# Revit family: LAMP_FIL 70 PRISMATIC RECESSED
name_source: partatom
category: Luminarias
revit_build: Autodesk Revit 2015 (Build: 20140606_1530(x64)
units: mm (PartAtom-declared; Revit-internal decimal feet)

## types (16) — shared parameters
CRI = 80
Cambio de temperatura de color de luz atenuada = <Ninguno>
Comentarios de tipo = Availability of switching between accessories through visibility parameters when placed in a project.
Fabricante = LAMP
Filtro de color = 16777215
Gear = Electronic
IEE = A+
IFC Clasificación = Light Fixture
Installation instructions = https://www.lamp.es
Insulation class = I
LED Lifetime = 50.000 L80 B10
Last update = 14/08/2020
Luminaire type = Indoor - Modular System
Lámpara = LED MID-POWER
MacAdam = 3
Manufacturer URL = http://www.lamp.es
Manufacturer country = Spain
Manufacturer name = LAMP
Material Difusor = LAMP_PC Difusor Prismático Fil
Model explanation = Availability of switching between accessories through visibility parameters when placed in a project.
Power Supply = 220-240V 50-60Hz
Product URL = https://www.lamp.es
Product datasheet = https://www.lamp.es
Protection rating = IP42, IK06
Type = MID POWER PHILIPS
Ángulo de inclinación = 90,00°

## per-type parameters (varying)
| type | Archivo de red fotométrica | Descripción | Dimensions | Efficacy | Finish | Longitud | Longitud de línea de emisión | Material Perfil | Modelo | Plum | Power | Product code | Recessed dimensions | UniClass 1.4 Code | UniClass 2.0 Code | Weight |
| 1162MM 2600LM 3000K WHITE | 14741700.IES | FIL 70 PRISM REC 2600 WW WH. | 1162 x 89 x 70 mm | 114 lm/W | Matt white | 1162 mm  [stored 3.81234 ft] | 1162 mm  [stored 3.81234 ft] | LAMP_Aluminio Perfil Fil BL | F71RE120LOPR830NW | 19 W | 17 W | F71RE120LOPR830NW | 1174 x 78 x 85 mm | F71RE120LOPR830NW | F71RE120LOPR830NW | 2,77 kg |
| 1162MM 2600LM 3000K GREY | 14741703.IES | FIL 70 PRISM REC 2600 WW GR. | 1162 x 89 x 70 mm | 114 lm/W | Gloss grey | 1162 mm  [stored 3.81234 ft] | 1162 mm  [stored 3.81234 ft] | LAMP_Aluminio Perfil Fil GR | F71RE120LOPR830NG
F71RE120LOPR830NG | 19 W | 17 W | F71RE120LOPR830NG
F71RE120LOPR830NG | 1174 x 78 x 85 mm | F71RE120LOPR830NG
F71RE120LOPR830NG | F71RE120LOPR830NG
F71RE120LOPR830NG | 2,77 kg |
| 1162MM 2600LM 4000K WHITE | 14740700.IES | FIL 70 OPAL REC 2600 NW WH. | 1162 x 89 x 70 mm | 119 lm/W | Matt white | 1162 mm  [stored 3.81234 ft] | 1162 mm  [stored 3.81234 ft] | LAMP_Aluminio Perfil Fil BL | F71RE120LOPR840NW | 19 W | 17 W | F71RE120LOPR840NW | 1174 x 78 x 85 mm | F71RE120LOPR840NW | F71RE120LOPR840NW | 2,77 kg |
| 1162MM 2600LM 4000K GREY | 14740703.IES | FIL 70 PRISM REC 2600 NW GR. | 1162 x 89 x 70 mm | 119 lm/W | Gloss grey | 1162 mm  [stored 3.81234 ft] | 1162 mm  [stored 3.81234 ft] | LAMP_Aluminio Perfil Fil GR | F71RE120LOPR840NG | 19 W | 17 W | F71RE120LOPR840NG | 1174 x 78 x 85 mm | F71RE120LOPR840NG | F71RE120LOPR840NG | 2,77 kg |
| 1162MM 4400LM 3000K WHITE | 14741710.IES | FIL 70 PRISM REC 4400 WW WH. | 1162 x 89 x 70 mm | 117 lm/W | Matt white | 1162 mm  [stored 3.81234 ft] | 1162 mm  [stored 3.81234 ft] | LAMP_Aluminio Perfil Fil BL | F71RE120HOPR830NW | 31 W | 28 W | F71RE120HOPR830NW | 1174 x 78 x 85 mm | F71RE120HOPR830NW | F71RE120HOPR830NW | 2,77 kg |
| 1162MM 4400LM 3000K GREY | 14741713.IES | FIL 70 PRISM REC 4400 WW GR. | 1162 x 89 x 70 mm | 117 lm/W | Gloss grey | 1162 mm  [stored 3.81234 ft] | 1162 mm  [stored 3.81234 ft] | LAMP_Aluminio Perfil Fil GR | F71RE120HOPR830NG | 31 W | 28 W | F71RE120HOPR830NG | 1174 x 78 x 85 mm | F71RE120HOPR830NG | F71RE120HOPR830NG | 2,77 kg |
| 1162MM 4400LM 4000K WHITE | 14740710.IES | FIL 70 PRISM REC 4400 NW WH. | 1162 x 89 x 70 mm | 122 lm/W | Matt white | 1162 mm  [stored 3.81234 ft] | 1162 mm  [stored 3.81234 ft] | LAMP_Aluminio Perfil Fil BL | F71RE120HOPR840NW | 31 W | 28 W | F71RE120HOPR840NW | 1174 x 78 x 85 mm | F71RE120HOPR840NW | F71RE120HOPR840NW | 2,77 kg |
| 1162MM 4400LM 4000K GREY | 14740713.IES | FIL 70 PRISM REC 4400 NW GR. | 1162 x 89 x 70 mm | 122 lm/W | Gloss grey | 1162 mm  [stored 3.81234 ft] | 1162 mm  [stored 3.81234 ft] | LAMP_Aluminio Perfil Fil GR | F71RE120HOPR840NG | 31 W | 28 W | F71RE120HOPR840NG | 1174 x 78 x 85 mm | F71RE120HOPR840NG | F71RE120HOPR840NG | 2,77 kg |
| 1743MM 3900LM 3000K WHITE | 14741720.IES | FIL 70 PRISM REC 3900 WW WH. | 1743 x 89 x 70 mm | 124 lm/W | Matt white | 1743 mm  [stored 5.7185 ft] | 1743 mm  [stored 5.7185 ft] | LAMP_Aluminio Perfil Fil BL | F71RE170LOPR830NW | 30 W | 25 W | F71RE170LOPR830NW | 1755 x 78 x 85 mm | F71RE170LOPR830NW | F71RE170LOPR830NW | 4,43 kg |
| 1743MM 3900LM 3000K GREY | 14741723.IES | FIL 70 PRISM REC 3900 WW GR. | 1743 x 89 x 70 mm | 124 lm/W | Gloss grey | 1743 mm  [stored 5.7185 ft] | 1743 mm  [stored 5.7185 ft] | LAMP_Aluminio Perfil Fil GR | F71RE170LOPR830NG | 30 W | 25 W | F71RE170LOPR830NG | 1755 x 78 x 85 mm | F71RE170LOPR830NG | F71RE170LOPR830NG | 4,43 kg |
| 1743MM 3900LM 4000K WHITE | 14740720.IES | FIL 70 PRISM REC 3900 NW WH. | 1743 x 89 x 70 mm | 129 lm/W | Matt white | 1743 mm  [stored 5.7185 ft] | 1743 mm  [stored 5.7185 ft] | LAMP_Aluminio Perfil Fil BL | F71RE170LOPR840NW | 30 W | 25 W | F71RE170LOPR840NW | 1755 x 78 x 85 mm | F71RE170LOPR840NW | F71RE170LOPR840NW | 4,43 kg |
| 1743MM 3900LM 4000K GREY | 14740723.IES | FIL 70 PRISM REC 3900 NW GR. | 1743 x 89 x 70 mm | 129 lm/W | Gloss grey | 1743 mm  [stored 5.7185 ft] | 1743 mm  [stored 5.7185 ft] | LAMP_Aluminio Perfil Fil GR | F71RE170LOPR840NG | 30 W | 25 W | F71RE170LOPR840NG | 1755 x 78 x 85 mm | F71RE170LOPR840NG | F71RE170LOPR840NG | 4,43 kg |
| 1743MM 6600LM 3000K WHITE | 14741730.IES | FIL 70 PRISM REC 6600 WW WH. | 1743 x 89 x 70 mm | 123 lm/W | Matt white | 1743 mm  [stored 5.7185 ft] | 1743 mm  [stored 5.7185 ft] | LAMP_Aluminio Perfil Fil BL | F71RE170HOPR830NW | 46 W | 41 W | F71RE170HOPR830NW | 1755 x 78 x 85 mm | F71RE170HOPR830NW | F71RE170HOPR830NW | 4,43 kg |
| 1743MM 6600LM 3000K GREY | 14741733.IES | FIL 70 PRISM REC 6600 WW GR. | 1743 x 89 x 70 mm | 123 lm/W | Gloss grey | 1743 mm  [stored 5.7185 ft] | 1743 mm  [stored 5.7185 ft] | LAMP_Aluminio Perfil Fil GR | F71RE170HOPR830NG | 46 W | 41 W | F71RE170HOPR830NG | 1755 x 78 x 85 mm | F71RE170HOPR830NG | F71RE170HOPR830NG | 4,43 kg |
| 1743MM 6600LM 4000K WHITE | 14740730.IES | FIL 70 PRISM REC 6600 NW WH. | 1743 x 89 x 70 mm | 127 lm/W | Matt white | 1743 mm  [stored 5.7185 ft] | 1743 mm  [stored 5.7185 ft] | LAMP_Aluminio Perfil Fil BL | F71RE170HOPR840NW | 46 W | 41 W | F71RE170HOPR840NW | 1755 x 78 x 85 mm | F71RE170HOPR840NW | F71RE170HOPR840NW | 4,43 kg |
| 1743MM 6600LM 4000K GREY | 14740733.IES | FIL 70 PRISM REC 6600 NW GR. | 1743 x 89 x 70 mm | 127 lm/W | Gloss grey | 1743 mm  [stored 5.7185 ft] | 1743 mm  [stored 5.7185 ft] | LAMP_Aluminio Perfil Fil GR | F71RE170HOPR840NG | 46 W | 41 W | F71RE170HOPR840NG | 1755 x 78 x 85 mm | F71RE170HOPR840NG | F71RE170HOPR840NG | 4,43 kg |

note: [stored X ft] marks values corroborated as IEEE doubles in the binary element streams (Revit-internal decimal feet)

## geometry (parser evidence)
native form markers: Blend x10
no freeform markers — native parametric forms only
